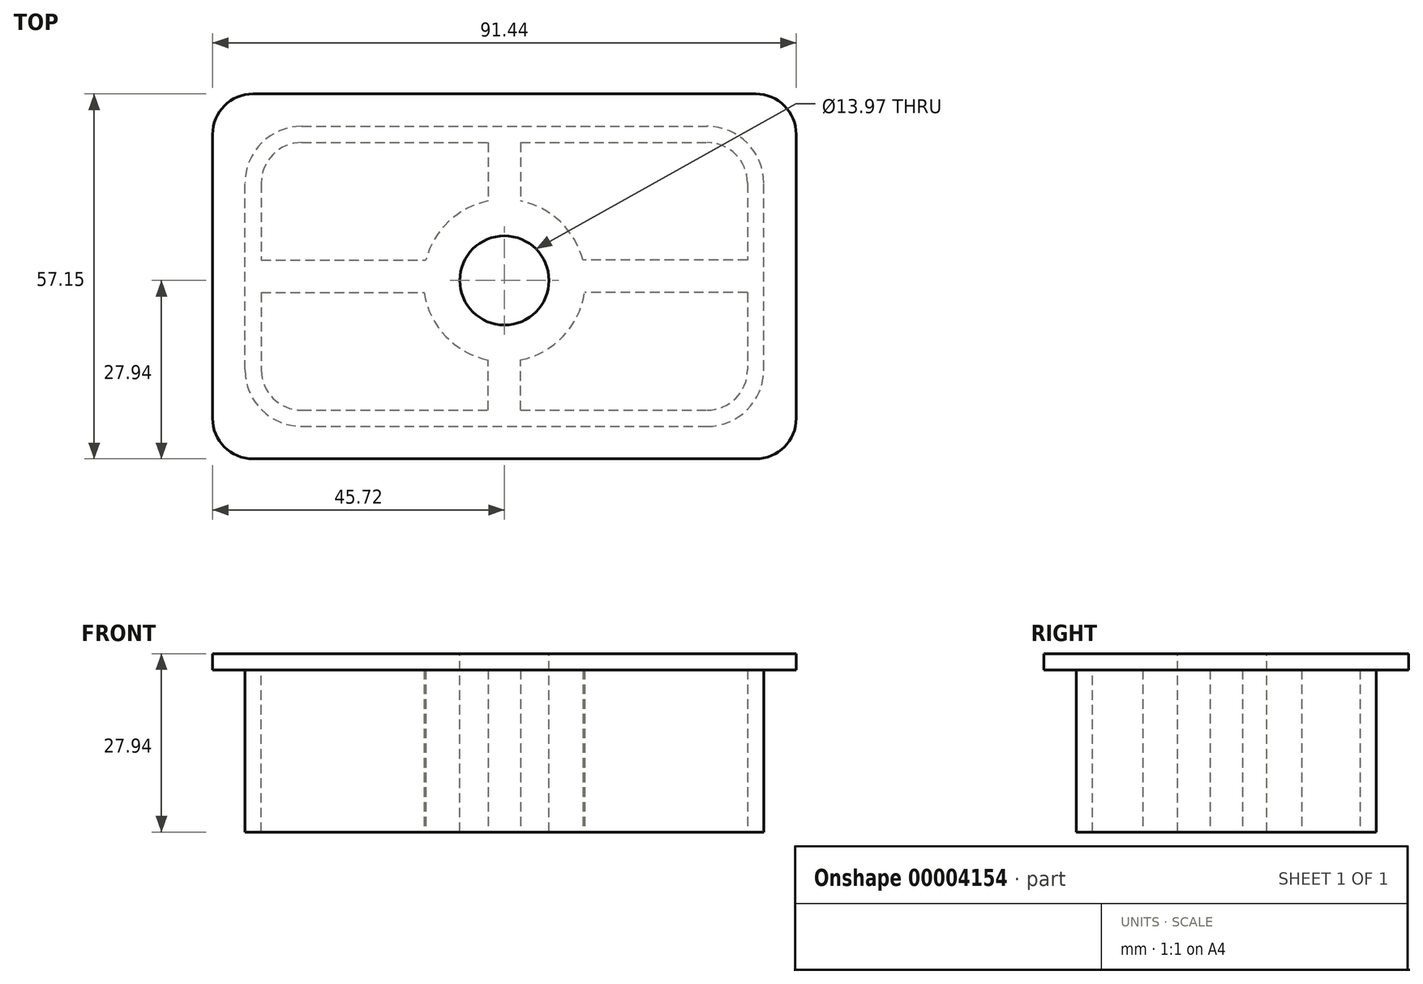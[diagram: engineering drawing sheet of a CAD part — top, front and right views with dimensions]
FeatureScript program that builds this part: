
annotation { "Feature Type Name" : "Feature", "Feature Type Description" : "" }
export const myFeature = defineFeature(function(context is Context, id is Id, definition is map)
    precondition{}
    {
        {
            var Q0;
            Q0=qCreatedBy(makeId("Top.planeOp"),FACE);
            var sketch = newSketch(context, id + "F0", { "sketchPlane" : qUnion([Q0])});
            skLineSegment(sketch, "E0.bottom", {"start": v(8.89, 0) * mm, "end": v(72.4, 0) * mm});
            skLineSegment(sketch, "E0.top", {"start": v(8.89, 47) * mm, "end": v(72.4, 47) * mm});
            skLineSegment(sketch, "E0.left", {"start": v(0, 8.89) * mm, "end": v(0, 38.1) * mm});
            skLineSegment(sketch, "E0.right", {"start": v(81.28, 8.9) * mm, "end": v(81.28, 38.1) * mm});
            skPoint(sketch, "E1.visualSharp", {"position": v(0, 47) * mm});
            skArc(sketch, "E1.filletArc", {"start": v(8.89, 47) * mm, "mid": v(2.6, 44.39) * mm, "end": v(0, 38.1) * mm});
            skPoint(sketch, "E2.visualSharp", {"position": v(0, 0) * mm});
            skArc(sketch, "E2.filletArc", {"start": v(0, 8.89) * mm, "mid": v(2.6, 2.6) * mm, "end": v(8.89, 0) * mm});
            skPoint(sketch, "E3.visualSharp", {"position": v(81.28, 0) * mm});
            skArc(sketch, "E3.filletArc", {"start": v(72.4, 0) * mm, "mid": v(78.68, 2.6) * mm, "end": v(81.28, 8.9) * mm});
            skPoint(sketch, "E4.visualSharp", {"position": v(81.28, 47) * mm});
            skArc(sketch, "E4.filletArc", {"start": v(81.28, 38.1) * mm, "mid": v(78.68, 44.39) * mm, "end": v(72.4, 47) * mm});
            skSolve(sketch);
        }
        {
            var Q0;
            Q0=makeQuery(id+"F0.imprint","IMPRINT",FACE,{"disambiguationData":[TD([[makeQuery(id+"F0.imprint","IMPRINT",EDGE,{"derivedFrom":sQuery(id+"F0.wireOp",EDGE,"E0.bottom")}),1.0]])]});
            extrude(context, id + "F1", {"entities" : qUnion([Q0]), "depth" : 25.4 * mm});
        }
        {
            var Q0;
            Q0=makeQuery(id+"F1.opExtrude","CAP_FACE",FACE,{"disambiguationData":[OSD([sQuery(id+"F0.wireOp",EDGE,"E0.bottom"),sQuery(id+"F0.wireOp",EDGE,"E0.top"),sQuery(id+"F0.wireOp",EDGE,"E0.left"),sQuery(id+"F0.wireOp",EDGE,"E0.right"),sQuery(id+"F0.wireOp",EDGE,"E1.filletArc"),sQuery(id+"F0.wireOp",EDGE,"E2.filletArc"),sQuery(id+"F0.wireOp",EDGE,"E3.filletArc"),sQuery(id+"F0.wireOp",EDGE,"E4.filletArc")])],"isStart":false});
            var sketch = newSketch(context, id + "F2", { "sketchPlane" : qUnion([Q0])});
            skLineSegment(sketch, "E5.bottom", {"start": v(1.27, -5.08) * mm, "end": v(80.01, -5.08) * mm});
            skLineSegment(sketch, "E5.top", {"start": v(1.27, 52.07) * mm, "end": v(80.01, 52.07) * mm});
            skLineSegment(sketch, "E5.left", {"start": v(-5.08, 1.27) * mm, "end": v(-5.08, 45.72) * mm});
            skLineSegment(sketch, "E5.right", {"start": v(86.36, 1.27) * mm, "end": v(86.36, 45.72) * mm});
            skPoint(sketch, "E6.visualSharp", {"position": v(-5.08, 52.07) * mm});
            skArc(sketch, "E6.filletArc", {"start": v(1.27, 52.07) * mm, "mid": v(-3.22, 50.21) * mm, "end": v(-5.08, 45.72) * mm});
            skPoint(sketch, "E7.visualSharp", {"position": v(-5.08, -5.08) * mm});
            skArc(sketch, "E7.filletArc", {"start": v(-5.08, 1.27) * mm, "mid": v(-3.22, -3.22) * mm, "end": v(1.27, -5.08) * mm});
            skPoint(sketch, "E8.visualSharp", {"position": v(86.36, -5.08) * mm});
            skArc(sketch, "E8.filletArc", {"start": v(80.01, -5.08) * mm, "mid": v(84.5, -3.22) * mm, "end": v(86.36, 1.27) * mm});
            skPoint(sketch, "E9.visualSharp", {"position": v(86.36, 52.07) * mm});
            skArc(sketch, "E9.filletArc", {"start": v(86.36, 45.72) * mm, "mid": v(84.5, 50.21) * mm, "end": v(80.01, 52.07) * mm});
            skSolve(sketch);
        }
        {
            var Q0;
            Q0 = qSketchRegion(id + "F2", true);
            extrude(context, id + "F3", {"entities" : qUnion([Q0]), "operationType" : NewBodyOperationType.ADD, "depth" : 2.54 * mm});
        }
        {
            var Q0;
            Q0=makeQuery(id+"F3.opExtrude","CAP_FACE",FACE,{"disambiguationData":[OSD([sQuery(id+"F2.wireOp",EDGE,"E5.bottom"),sQuery(id+"F2.wireOp",EDGE,"E5.top"),sQuery(id+"F2.wireOp",EDGE,"E5.left"),sQuery(id+"F2.wireOp",EDGE,"E5.right"),sQuery(id+"F2.wireOp",EDGE,"E6.filletArc"),sQuery(id+"F2.wireOp",EDGE,"E7.filletArc"),sQuery(id+"F2.wireOp",EDGE,"E8.filletArc"),sQuery(id+"F2.wireOp",EDGE,"E9.filletArc")])],"isStart":false});
            var sketch = newSketch(context, id + "F4", { "sketchPlane" : qUnion([Q0])});
            skCircle(sketch, "E10", {"center": v(40.64, 22.86) * mm, "radius": 6.99 * mm});
            skSolve(sketch);
        }
        {
            var Q0;
            Q0 = qSketchRegion(id + "F4", true);
            extrude(context, id + "F5", {"entities" : qUnion([Q0]), "operationType" : NewBodyOperationType.REMOVE, "oppositeDirection" : true, "depth" : 50.8 * mm});
        }
        {
            var Q0;
            Q0=makeQuery(id+"F1.opExtrude","CAP_FACE",FACE,{"disambiguationData":[OSD([sQuery(id+"F0.wireOp",EDGE,"E0.bottom"),sQuery(id+"F0.wireOp",EDGE,"E0.top"),sQuery(id+"F0.wireOp",EDGE,"E0.left"),sQuery(id+"F0.wireOp",EDGE,"E0.right"),sQuery(id+"F0.wireOp",EDGE,"E1.filletArc"),sQuery(id+"F0.wireOp",EDGE,"E2.filletArc"),sQuery(id+"F0.wireOp",EDGE,"E3.filletArc"),sQuery(id+"F0.wireOp",EDGE,"E4.filletArc")])],"isStart":true});
            var sketch = newSketch(context, id + "F6", { "sketchPlane" : qUnion([Q0])});
            skLineSegment(sketch, "E11.bottom", {"start": v(8.9, -44.45) * mm, "end": v(72.4, -44.45) * mm});
            skLineSegment(sketch, "E11.top", {"start": v(8.9, -2.54) * mm, "end": v(72.4, -2.54) * mm});
            skLineSegment(sketch, "E11.left", {"start": v(2.54, -38.1) * mm, "end": v(2.54, -8.9) * mm});
            skLineSegment(sketch, "E11.right", {"start": v(78.74, -38.1) * mm, "end": v(78.74, -8.9) * mm});
            skPoint(sketch, "E12.visualSharp", {"position": v(2.54, -2.54) * mm});
            skArc(sketch, "E12.filletArc", {"start": v(8.9, -2.54) * mm, "mid": v(4.4, -4.4) * mm, "end": v(2.54, -8.9) * mm});
            skPoint(sketch, "E13.visualSharp", {"position": v(78.74, -2.54) * mm});
            skArc(sketch, "E13.filletArc", {"start": v(78.74, -8.9) * mm, "mid": v(76.88, -4.4) * mm, "end": v(72.4, -2.54) * mm});
            skPoint(sketch, "E14.visualSharp", {"position": v(78.74, -44.45) * mm});
            skArc(sketch, "E14.filletArc", {"start": v(72.4, -44.45) * mm, "mid": v(76.88, -42.6) * mm, "end": v(78.74, -38.1) * mm});
            skPoint(sketch, "E15.visualSharp", {"position": v(2.54, -44.45) * mm});
            skArc(sketch, "E15.filletArc", {"start": v(2.54, -38.1) * mm, "mid": v(4.4, -42.6) * mm, "end": v(8.9, -44.45) * mm});
            skCircle(sketch, "E16", {"center": v(40.64, -22.86) * mm, "radius": 12.7 * mm});
            skLineSegment(sketch, "E17", {"start": v(40.64, 14.7) * mm, "end": v(40.64, -58.6) * mm, "construction": true});
            skLineSegment(sketch, "E18", {"start": v(-10.06, -22.86) * mm, "end": v(91.5, -22.86) * mm, "construction": true});
            skSolve(sketch);
        }
        {
            var Q0;
            Q0 = qSketchRegion(id + "F6", true);
            extrude(context, id + "F7", {"entities" : qUnion([Q0]), "operationType" : NewBodyOperationType.REMOVE, "oppositeDirection" : true, "depth" : 25.4 * mm});
        }
        {
            var Q0;
            {var subQ0=sQuery(id+"F0.wireOp",EDGE,"E0.bottom");var subQ1=sQuery(id+"F0.wireOp",EDGE,"E0.top");var subQ2=sQuery(id+"F0.wireOp",EDGE,"E0.left");var subQ3=sQuery(id+"F0.wireOp",EDGE,"E0.right");var subQ4=sQuery(id+"F0.wireOp",EDGE,"E1.filletArc");var subQ5=sQuery(id+"F0.wireOp",EDGE,"E2.filletArc");var subQ6=sQuery(id+"F0.wireOp",EDGE,"E3.filletArc");var subQ7=sQuery(id+"F0.wireOp",EDGE,"E4.filletArc");Q0=makeQuery(id+"F7.boolean.opBoolean","SPLIT",FACE,{"disambiguationData":[TD([makeQuery(id+"F1.opExtrude","SWEPT_FACE",FACE,{"disambiguationData":[OSD([subQ0])]})])],"derivedFrom":makeQuery(id+"F1.opExtrude","CAP_FACE",FACE,{"disambiguationData":[OSD([subQ0,subQ1,subQ2,subQ3,subQ4,subQ5,subQ6,subQ7])],"isStart":true})});}
            var sketch = newSketch(context, id + "F8", { "sketchPlane" : qUnion([Q0])});
            skLineSegment(sketch, "E19", {"start": v(40.64, 0) * mm, "end": v(40.64, -47) * mm, "construction": true});
            skLineSegment(sketch, "E20", {"start": v(2.54, -23.5) * mm, "end": v(78.74, -23.5) * mm, "construction": true});
            skLineSegment(sketch, "E21", {"start": v(32.63, 0) * mm, "end": v(32.63, -2.54) * mm, "construction": true});
            skLineSegment(sketch, "E22", {"start": v(32.63, -2.54) * mm, "end": v(32.63, -1.27) * mm, "construction": true});
            skLineSegment(sketch, "E23", {"start": v(32.63, -1.27) * mm, "end": v(48.58, -1.27) * mm, "construction": true});
            skLineSegment(sketch, "E24", {"start": v(2.54, -28.57) * mm, "end": v(0, -28.57) * mm, "construction": true});
            skLineSegment(sketch, "E25", {"start": v(0, -28.57) * mm, "end": v(1.27, -28.57) * mm, "construction": true});
            skLineSegment(sketch, "E26", {"start": v(1.27, -28.57) * mm, "end": v(1.27, -18.95) * mm, "construction": true});
            skLineSegment(sketch, "E27", {"start": v(81.28, -28.94) * mm, "end": v(78.74, -28.94) * mm, "construction": true});
            skLineSegment(sketch, "E28", {"start": v(78.74, -28.94) * mm, "end": v(80.01, -28.94) * mm});
            skLineSegment(sketch, "E29", {"start": v(80.01, -28.94) * mm, "end": v(80.01, -18.03) * mm, "construction": true});
            skLineSegment(sketch, "E30", {"start": v(29.98, -44.45) * mm, "end": v(29.98, -47) * mm, "construction": true});
            skLineSegment(sketch, "E31", {"start": v(29.98, -47) * mm, "end": v(29.98, -45.72) * mm, "construction": true});
            skLineSegment(sketch, "E32", {"start": v(29.98, -45.72) * mm, "end": v(48.67, -45.72) * mm, "construction": true});
            skLineSegment(sketch, "E33.bottom", {"start": v(38.1, -1.27) * mm, "end": v(43.18, -1.27) * mm});
            skLineSegment(sketch, "E33.top", {"start": v(38.1, -11.82) * mm, "end": v(43.18, -11.82) * mm});
            skLineSegment(sketch, "E33.left", {"start": v(38.1, -1.27) * mm, "end": v(38.1, -11.82) * mm});
            skLineSegment(sketch, "E33.right", {"start": v(43.18, -1.27) * mm, "end": v(43.18, -11.82) * mm});
            skLineSegment(sketch, "E34.bottom", {"start": v(38.1, -45.72) * mm, "end": v(43.18, -45.72) * mm});
            skLineSegment(sketch, "E34.top", {"start": v(38.1, -31.92) * mm, "end": v(43.18, -31.92) * mm});
            skLineSegment(sketch, "E34.left", {"start": v(38.1, -45.72) * mm, "end": v(38.1, -31.92) * mm});
            skLineSegment(sketch, "E34.right", {"start": v(43.18, -45.72) * mm, "end": v(43.18, -31.92) * mm});
            skLineSegment(sketch, "E35.bottom", {"start": v(80.01, -20.96) * mm, "end": v(49.43, -20.96) * mm});
            skLineSegment(sketch, "E35.top", {"start": v(80.01, -26.04) * mm, "end": v(49.43, -26.04) * mm});
            skLineSegment(sketch, "E35.left", {"start": v(80.01, -20.96) * mm, "end": v(80.01, -26.04) * mm});
            skLineSegment(sketch, "E35.right", {"start": v(49.43, -20.96) * mm, "end": v(49.43, -26.04) * mm});
            skLineSegment(sketch, "E36.bottom", {"start": v(1.27, -20.96) * mm, "end": v(29.43, -20.96) * mm});
            skLineSegment(sketch, "E36.top", {"start": v(1.27, -26.04) * mm, "end": v(29.43, -26.04) * mm});
            skLineSegment(sketch, "E36.left", {"start": v(1.27, -20.96) * mm, "end": v(1.27, -26.04) * mm});
            skLineSegment(sketch, "E36.right", {"start": v(29.43, -20.96) * mm, "end": v(29.43, -26.04) * mm});
            skSolve(sketch);
        }
        {
            var Q0;
            Q0 = qSketchRegion(id + "F8", true);
            extrude(context, id + "F9", {"entities" : qUnion([Q0]), "operationType" : NewBodyOperationType.ADD, "oppositeDirection" : true, "depth" : 26.67 * mm});
        }
    });
